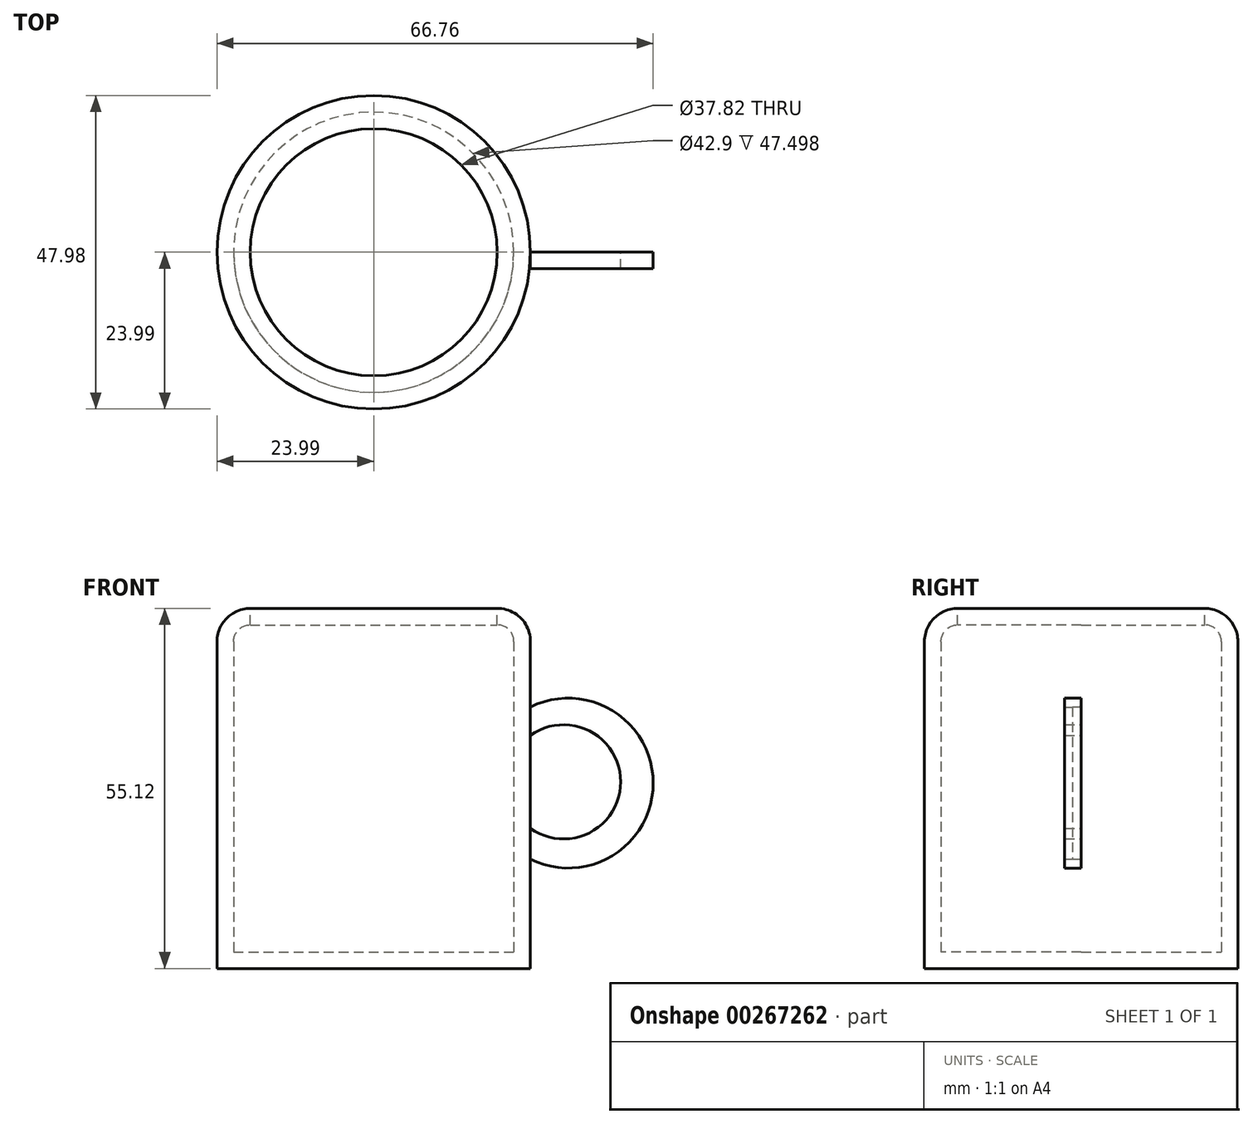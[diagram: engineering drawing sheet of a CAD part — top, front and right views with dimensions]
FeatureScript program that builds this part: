
annotation { "Feature Type Name" : "Feature", "Feature Type Description" : "" }
export const myFeature = defineFeature(function(context is Context, id is Id, definition is map)
    precondition{}
    {
        {
            var Q0;
            Q0=qCreatedBy(makeId("Top.planeOp"),FACE);
            var sketch = newSketch(context, id + "F0", { "sketchPlane" : qUnion([Q0])});
            skCircle(sketch, "E0", {"center": v(0, 0) * mm, "radius": 24 * mm});
            skSolve(sketch);
        }
        {
            var Q0;
            Q0 = qSketchRegion(id + "F0", true);
            extrude(context, id + "F1", {"entities" : qUnion([Q0]), "depth" : 55.12 * mm});
        }
        {
            var Q0;
            Q0=makeQuery(id+"F1.opExtrude","CAP_FACE",FACE,{"disambiguationData":[OSD([sQuery(id+"F0.wireOp",EDGE,"E0")])],"isStart":false});
            fillet(context, id + "F2", {"entities" : qUnion([Q0]), "radius" : 5.08 * mm, "tangentPropagation" : true, "allowEdgeOverflow" : false});
        }
        {
            var Q0;
            Q0=makeQuery(id+"F1.opExtrude","CAP_FACE",FACE,{"disambiguationData":[OSD([sQuery(id+"F0.wireOp",EDGE,"E0")])],"isStart":false});
            shell(context, id + "F3", {"entities" : qUnion([Q0]), "thickness" : 2.54 * mm});
        }
        {
            var Q0;
            Q0=qCreatedBy(makeId("Front.planeOp"),FACE);
            var sketch = newSketch(context, id + "F4", { "sketchPlane" : qUnion([Q0])});
            skLineSegment(sketch, "E1", {"start": v(23.95, 40) * mm, "end": v(23.95, 16.74) * mm});
            skArc(sketch, "E2", {"start": v(23.95, 16.74) * mm, "mid": v(42.77, 28.37) * mm, "end": v(23.95, 40) * mm});
            skSolve(sketch);
        }
        {
            var Q0;
            Q0 = qSketchRegion(id + "F4", true);
            extrude(context, id + "F5", {"entities" : qUnion([Q0]), "operationType" : NewBodyOperationType.ADD, "depth" : 2.54 * mm});
        }
        {
            var Q0;
            Q0=qCreatedBy(makeId("Front.planeOp"),FACE);
            var sketch = newSketch(context, id + "F6", { "sketchPlane" : qUnion([Q0])});
            skLineSegment(sketch, "E3", {"start": v(23.98, 35.67) * mm, "end": v(23.98, 21.45) * mm});
            skArc(sketch, "E4", {"start": v(23.98, 21.45) * mm, "mid": v(37.8, 28.56) * mm, "end": v(23.98, 35.67) * mm});
            skSolve(sketch);
        }
        {
            var Q0;
            Q0 = qSketchRegion(id + "F6", true);
            extrude(context, id + "F7", {"entities" : qUnion([Q0]), "operationType" : NewBodyOperationType.REMOVE, "depth" : 4.14 * mm});
        }
    });
